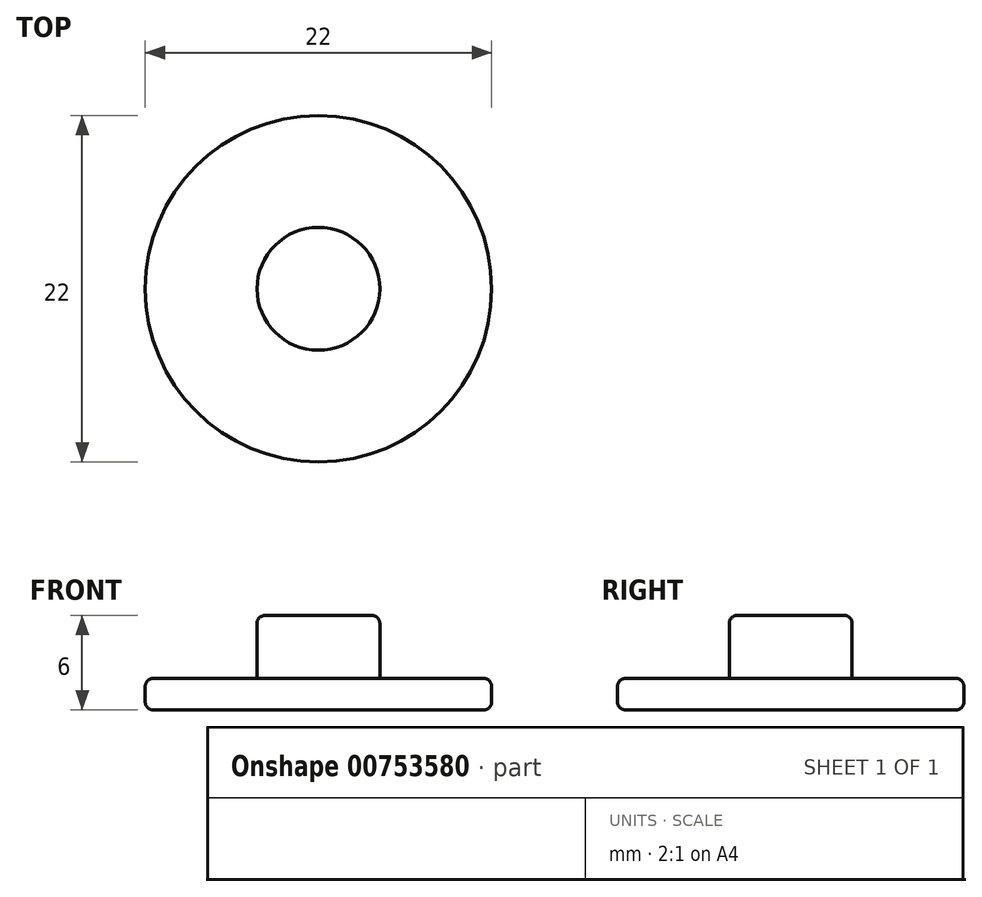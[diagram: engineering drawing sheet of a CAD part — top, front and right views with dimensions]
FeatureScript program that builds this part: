
annotation { "Feature Type Name" : "Feature", "Feature Type Description" : "" }
export const myFeature = defineFeature(function(context is Context, id is Id, definition is map)
    precondition{}
    {
        {
            var Q0;
            Q0=qCreatedBy(makeId("Top.planeOp"),FACE);
            var sketch = newSketch(context, id + "F0", { "sketchPlane" : qUnion([Q0])});
            skCircle(sketch, "E0", {"center": v(0, 0) * mm, "radius": 11 * mm});
            skSolve(sketch);
        }
        {
            var Q0;
            Q0=makeQuery(id+"F0.imprint","IMPRINT",FACE,{"disambiguationData":[TD([[makeQuery(id+"F0.imprint","IMPRINT",EDGE,{"derivedFrom":sQuery(id+"F0.wireOp",EDGE,"3279ac41-825b-4453-ad9c-405e0f383d23")}),-1.0]])]});
            var Q1;
            Q1=makeQuery(id+"F0.imprint","IMPRINT",FACE,{"disambiguationData":[TD([[makeQuery(id+"F0.imprint","IMPRINT",EDGE,{"derivedFrom":sQuery(id+"F0.wireOp",EDGE,"E0")}),1.0]])]});
            extrude(context, id + "F1", {"entities" : qUnion([Q0, Q1]), "depth" : 2 * mm, "offsetDistance" : 25.4 * mm});
        }
        {
            var Q0;
            Q0=qCreatedBy(makeId("Top.planeOp"),FACE);
            var sketch = newSketch(context, id + "F2", { "sketchPlane" : qUnion([Q0])});
            skCircle(sketch, "E1", {"center": v(0, 0) * mm, "radius": 3.9 * mm});
            skSolve(sketch);
        }
        {
            var Q0;
            Q0=makeQuery(id+"F2.imprint","IMPRINT",FACE,{"disambiguationData":[TD([[makeQuery(id+"F2.imprint","IMPRINT",EDGE,{"derivedFrom":sQuery(id+"F2.wireOp",EDGE,"E1")}),1.0]])]});
            extrude(context, id + "F3", {"entities" : qUnion([Q0]), "operationType" : NewBodyOperationType.ADD, "depth" : 6 * mm, "offsetDistance" : 25.4 * mm});
        }
        {
            var Q0;
            Q0=makeQuery(id+"F1.opExtrude","CAP_EDGE",EDGE,{"disambiguationData":[OSD([sQuery(id+"F0.wireOp",EDGE,"E0")])],"isStart":false});
            var Q1;
            Q1=makeQuery(id+"F1.opExtrude","CAP_EDGE",EDGE,{"disambiguationData":[OSD([sQuery(id+"F0.wireOp",EDGE,"E0")])],"isStart":true});
            var Q2;
            Q2=makeQuery(id+"F3.opExtrude","CAP_EDGE",EDGE,{"disambiguationData":[OSD([sQuery(id+"F2.wireOp",EDGE,"E1")])],"isStart":false});
            fillet(context, id + "F4", {"entities" : qUnion([Q0, Q1, Q2]), "radius" : .5 * mm, "tangentPropagation" : true, "allowEdgeOverflow" : false});
        }
    });
